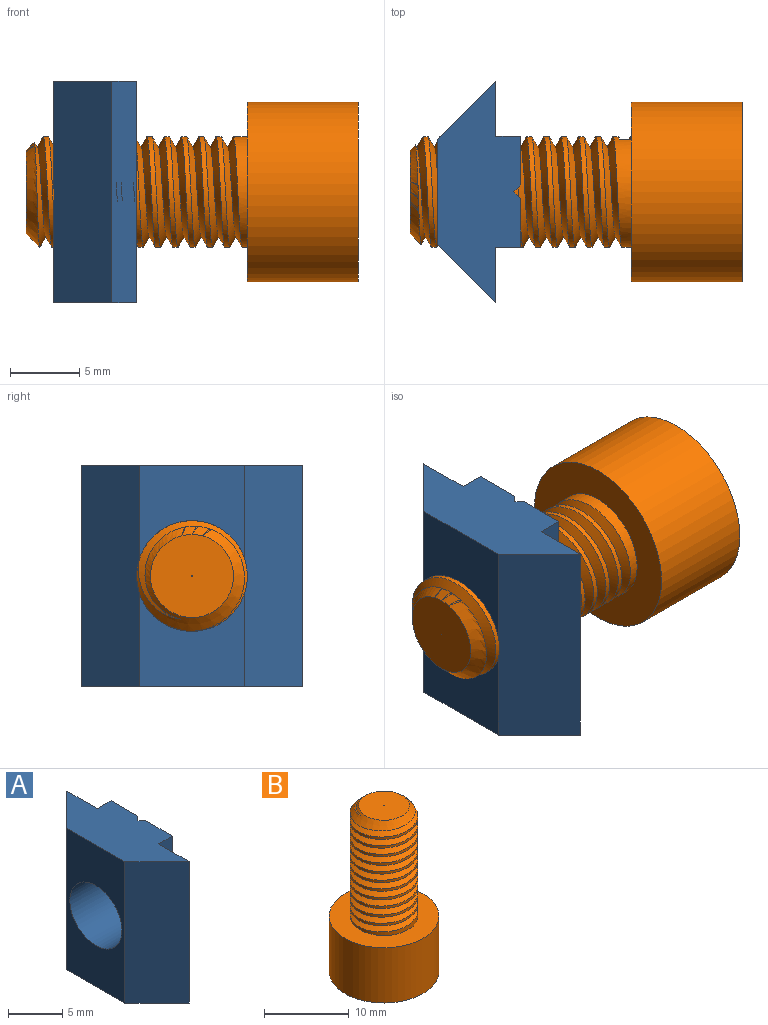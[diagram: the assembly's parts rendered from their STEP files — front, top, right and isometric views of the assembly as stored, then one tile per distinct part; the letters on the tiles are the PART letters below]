
ASSEMBLY  parts=2 mates=1
PART A: 16 faces, bbox 6x16x16 mm
  f0: plane 4.64x0.5mm, normal (0.71,0.71,0), area 3.3mm2, adj f6,f8,f14,f15
  f1: plane 4.64x0.5mm, normal (0.71,-0.71,0), area 3.3mm2, adj f7,f9,f13,f15
  f2: plane 16x7.6mm, normal (-1,0,0), area 85.3mm2, adj f3,f12,f13,f14,f15
  f3: plane 16x4.2mm, normal (-0.71,-0.71,0), area 95mm2, adj f2,f4,f13,f14
  f4: plane 16x4mm, normal (1,0,0), area 64mm2, adj f3,f5,f13,f14
  f5: plane 16x1.8mm, normal (0,-1,0), area 28.8mm2, adj f4,f6,f13,f14
  f6: plane 16x3.5mm, normal (1,0,0), area 41.2mm2, adj f0,f5,f7,f13,f14,f15
  f7: plane 4.64x0.5mm, normal (0.71,0.71,0), area 3.3mm2, adj f1,f6,f13,f15
  f8: plane 4.64x0.5mm, normal (0.71,-0.71,0), area 3.3mm2, adj f0,f9,f14,f15
  f9: plane 16x3.5mm, normal (1,0,0), area 41.2mm2, adj f1,f8,f10,f13,f14,f15
  f10: plane 16x1.8mm, normal (0,1,0), area 28.8mm2, adj f9,f11,f13,f14
  f11: plane 16x4mm, normal (1,0,0), area 64mm2, adj f10,f12,f13,f14
  f12: plane 16x4.2mm, normal (-0.71,0.71,0), area 95mm2, adj f2,f11,f13,f14
  f13: plane 16x6mm, normal (0,0,1), area 63.7mm2, adj f1,f2,f3,f4,f5,f6,f7,f9
  f14: plane 16x6mm, normal (0,0,-1), area 63.7mm2, adj f0,f2,f3,f4,f5,f6,f8,f9
  f15: cylinder r=3.4mm len=6.8mm, axis (-1,0,0), area 127.7mm2, adj f0,f1,f2,f6,f7,f8,f9
PART B: 17 faces, bbox 13x13x24.3 mm
  f0: plane 13x13mm, normal (0,0,-1), area 101.6mm2, adj f8,f9,f10,f11,f12,f13,f14
  f1: cylinder r=4mm len=15mm, axis (0,0,-1), area 125.8mm2, adj f3,f4,f5,f6,f7
  f2: plane 6x6mm, normal (0,0,1), area 28.3mm2, adj f3,f16
  f3: cone r=3mm half-angle=45deg, axis (0,0,-1), area 22mm2, adj f1,f2,f4,f6
  f4: bspline ~15.86x9.24mm, area 245.3mm2, adj f1,f3,f5,f6,f7
  f5: plane 0.89x0.74mm, normal (-0.95,0.31,0), area 0.3mm2, adj f1,f4,f6
  f6: bspline ~15.86x9.24mm, area 237.7mm2, adj f1,f3,f4,f5
  f7: plane 13x13mm, normal (0,0,1), area 82.4mm2, adj f1,f4,f8
  f8: cylinder r=6.5mm len=13mm, axis (0,0,1), area 326.7mm2, adj f0,f7
  f9: plane 5.9x3mm, normal (-0.5,0.87,0), area 20.4mm2, adj f0,f10,f14,f15
  f10: plane 5.9x3mm, normal (0.5,0.87,0), area 20.4mm2, adj f0,f9,f11,f15
  f11: plane 5.9x3.46mm, normal (1,0,0), area 20.4mm2, adj f0,f10,f12,f15
  f12: plane 5.9x3mm, normal (0.5,-0.87,0), area 20.4mm2, adj f0,f11,f13,f15
  f13: plane 5.9x3mm, normal (-0.5,-0.87,0), area 20.4mm2, adj f0,f12,f14,f15
  f14: plane 5.9x3.46mm, normal (-1,0,0), area 20.4mm2, adj f0,f9,f13,f15
  f15: plane 6.93x6mm, normal (0,0,-1), area 31.2mm2, adj f9,f10,f11,f12,f13,f14,f16
  f16: cylinder r=0.01mm len=18.1mm, axis (0,0,-1), area 0.6mm2, adj f2,f15
PLACE A t=(-11.91,-0.36,4.38)mm
PLACE B rot(axis=(0,-1,0),90deg) t=(-3.91,-0.36,12.38)mm
MATE fastened B.f1 <-> A.f15  axis (-1,0,0) through (-19.91,-0.36,12.38)mm
